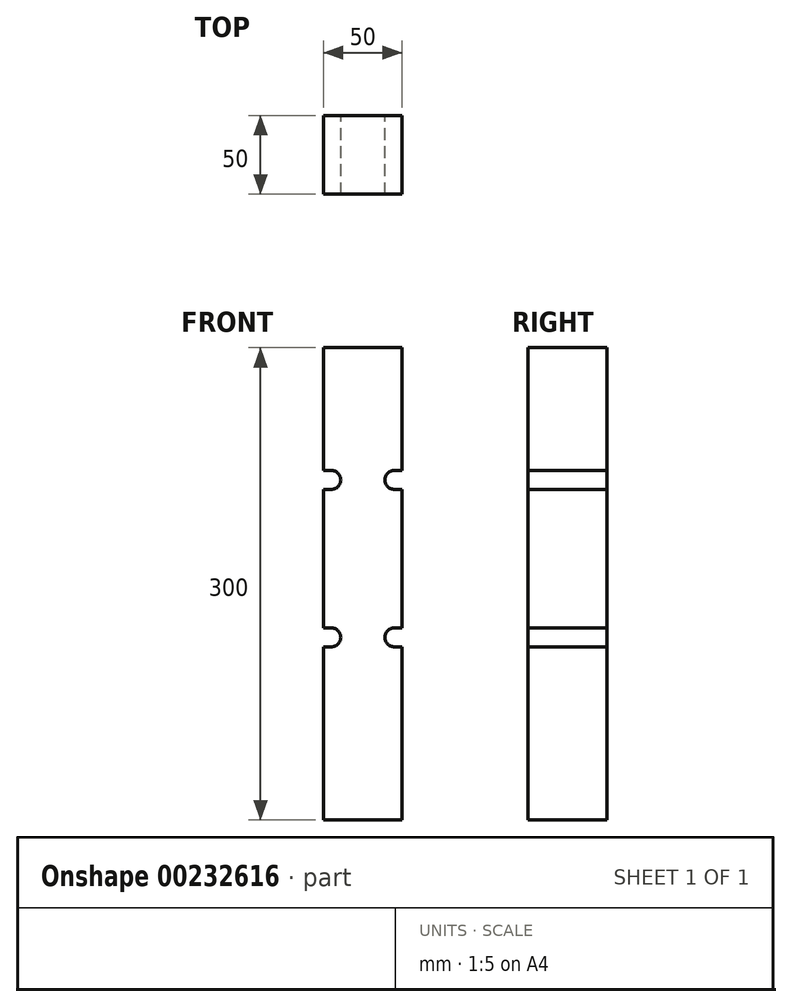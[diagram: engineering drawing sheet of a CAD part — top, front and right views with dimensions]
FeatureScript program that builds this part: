
annotation { "Feature Type Name" : "Feature", "Feature Type Description" : "" }
export const myFeature = defineFeature(function(context is Context, id is Id, definition is map)
    precondition{}
    {
        {
            var Q0;
            Q0=qCreatedBy(makeId("Top.planeOp"),FACE);
            var sketch = newSketch(context, id + "F0", { "sketchPlane" : qUnion([Q0])});
            skLineSegment(sketch, "E0.bottom", {"start": v(0, 0) * mm, "end": v(50, 0) * mm});
            skLineSegment(sketch, "E0.top", {"start": v(0, 50) * mm, "end": v(50, 50) * mm});
            skLineSegment(sketch, "E0.left", {"start": v(0, 0) * mm, "end": v(0, 50) * mm});
            skLineSegment(sketch, "E0.right", {"start": v(50, 0) * mm, "end": v(50, 50) * mm});
            skSolve(sketch);
        }
        {
            var Q0;
            Q0 = qSketchRegion(id + "F0", true);
            extrude(context, id + "F1", {"entities" : qUnion([Q0]), "depth" : 300 * mm});
        }
        {
            var Q0;
            Q0=makeQuery(id+"F1.opExtrude","SWEPT_FACE",FACE,{"disambiguationData":[OSD([sQuery(id+"F0.wireOp",EDGE,"E0.top")])]});
            var sketch = newSketch(context, id + "F2", { "sketchPlane" : qUnion([Q0])});
            skArc(sketch, "E1", {"start": v(-45, 210) * mm, "mid": v(-39, 216) * mm, "end": v(-45, 222) * mm});
            skArc(sketch, "E2", {"start": v(-5, 222) * mm, "mid": v(-11, 216) * mm, "end": v(-5, 210) * mm});
            skArc(sketch, "E3", {"start": v(-45, 110) * mm, "mid": v(-39, 116) * mm, "end": v(-45, 122) * mm});
            skArc(sketch, "E4", {"start": v(-5, 122) * mm, "mid": v(-11, 116) * mm, "end": v(-5, 110) * mm});
            skLineSegment(sketch, "E5", {"start": v(-50, 222) * mm, "end": v(-45, 222) * mm});
            skLineSegment(sketch, "E6.trimOffspring", {"start": v(-5, 222) * mm, "end": v(0, 222) * mm});
            skLineSegment(sketch, "E7", {"start": v(-50, 210) * mm, "end": v(-45, 210) * mm});
            skLineSegment(sketch, "E8.trimOffspring", {"start": v(-5, 210) * mm, "end": v(0, 210) * mm});
            skLineSegment(sketch, "E9", {"start": v(-50, 222) * mm, "end": v(-50, 210) * mm});
            skLineSegment(sketch, "E10", {"start": v(0, 222) * mm, "end": v(0, 210) * mm});
            skLineSegment(sketch, "E11", {"start": v(-50, 122) * mm, "end": v(-45, 122) * mm});
            skLineSegment(sketch, "E12", {"start": v(-50, 110) * mm, "end": v(-45, 110) * mm});
            skLineSegment(sketch, "E13", {"start": v(-50, 122) * mm, "end": v(-50, 110) * mm});
            skLineSegment(sketch, "E14", {"start": v(0, 122) * mm, "end": v(0, 110) * mm});
            skLineSegment(sketch, "E15.trimOffspring", {"start": v(-5, 122) * mm, "end": v(0, 122) * mm});
            skLineSegment(sketch, "E16.trimOffspring", {"start": v(-5, 110) * mm, "end": v(0, 110) * mm});
            skSolve(sketch);
        }
        {
            var Q0;
            Q0 = qSketchRegion(id + "F2", true);
            extrude(context, id + "F3", {"entities" : qUnion([Q0]), "operationType" : NewBodyOperationType.REMOVE, "endBound" : BoundingType.THROUGH_ALL, "oppositeDirection" : true, "depth" : 25 * mm});
        }
    });
